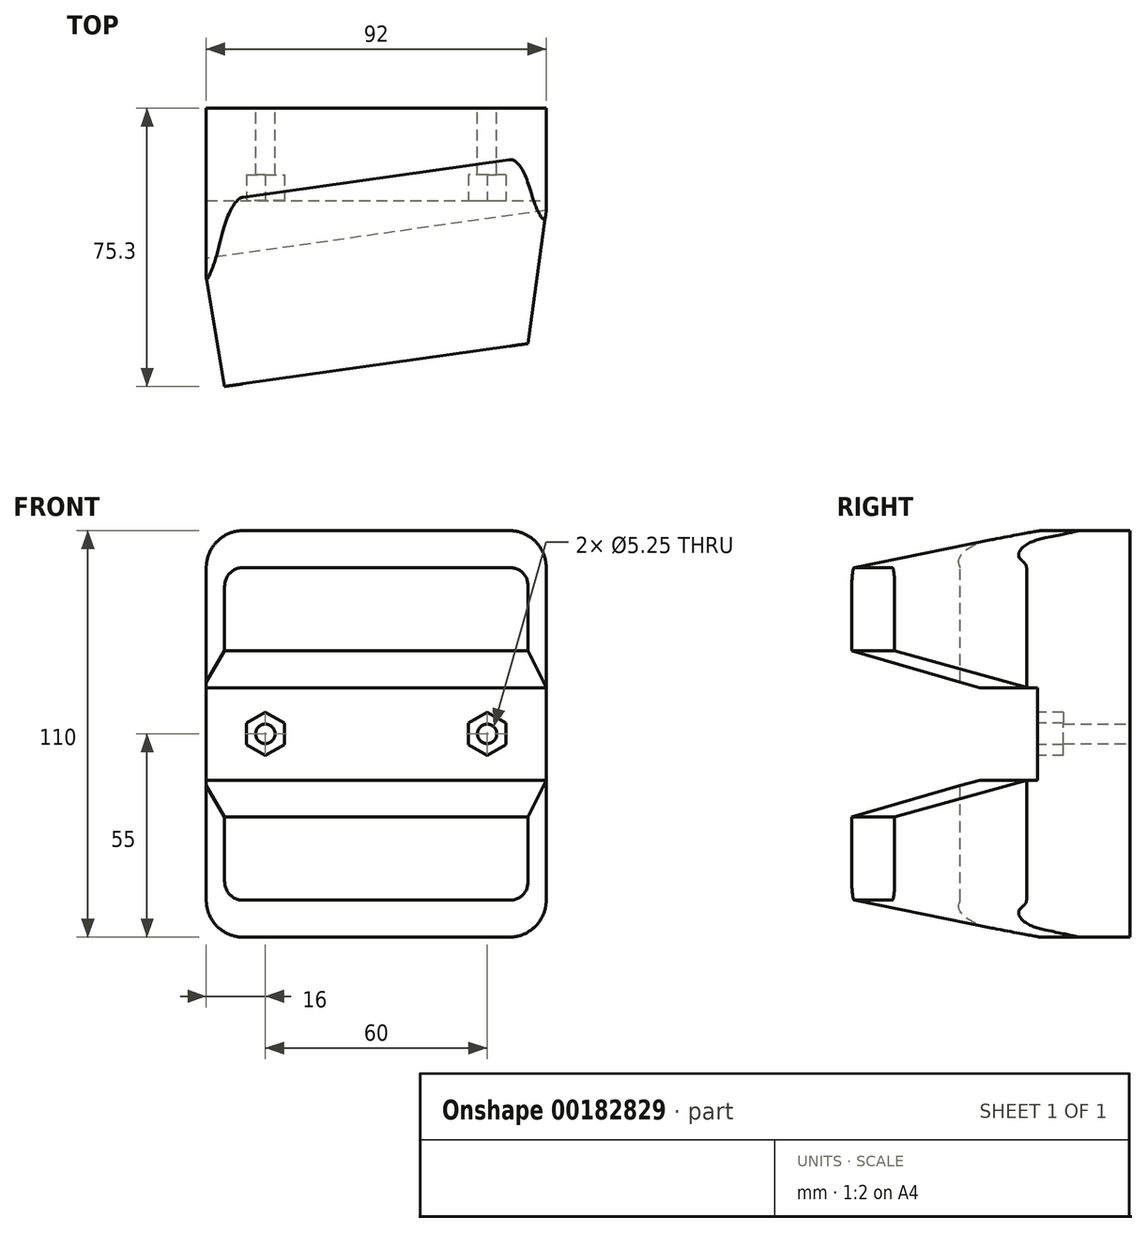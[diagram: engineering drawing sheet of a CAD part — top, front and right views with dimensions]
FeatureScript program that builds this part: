
annotation { "Feature Type Name" : "Feature", "Feature Type Description" : "" }
export const myFeature = defineFeature(function(context is Context, id is Id, definition is map)
    precondition{}
    {
        {
            var Q0;
            Q0=qCreatedBy(makeId("Top.planeOp"),FACE);
            var sketch = newSketch(context, id + "F0", { "sketchPlane" : qUnion([Q0])});
            skLineSegment(sketch, "E0", {"start": v(-46, 43.07) * mm, "end": v(46, 43.07) * mm});
            skLineSegment(sketch, "E1", {"start": v(46, 43.07) * mm, "end": v(46, -19.93) * mm});
            skLineSegment(sketch, "E2", {"start": v(46, -19.93) * mm, "end": v(-46, -32.93) * mm});
            skLineSegment(sketch, "E3", {"start": v(-46, -32.93) * mm, "end": v(-46, 43.07) * mm});
            skSolve(sketch);
        }
        {
            var Q0;
            Q0 = qSketchRegion(id + "F0", true);
            extrude(context, id + "F1", {"entities" : qUnion([Q0]), "depth" : 110 * mm});
        }
        {
            var Q0;
            Q0=makeQuery(id+"F1.opExtrude","SWEPT_FACE",FACE,{"disambiguationData":[OSD([sQuery(id+"F0.wireOp",EDGE,"E0")])]});
            cPlane(context, id + "F2", {"entities" : qUnion([Q0]), "cplaneType" : CPlaneType.OFFSET, "offset" : 25 * mm, "oppositeDirection" : true, "width" : 150 * mm, "height" : 150 * mm});
        }
        {
            var Q0;
            Q0=qCreatedBy(id+"F2.planeOp",FACE);
            var sketch = newSketch(context, id + "F3", { "sketchPlane" : qUnion([Q0])});
            skLineSegment(sketch, "E4.bottom", {"start": v(46, 67.5) * mm, "end": v(-46, 67.5) * mm});
            skLineSegment(sketch, "E4.top", {"start": v(46, 42.5) * mm, "end": v(-46, 42.5) * mm});
            skLineSegment(sketch, "E4.left", {"start": v(46, 67.5) * mm, "end": v(46, 42.5) * mm});
            skLineSegment(sketch, "E4.right", {"start": v(-46, 67.5) * mm, "end": v(-46, 42.5) * mm});
            skSolve(sketch);
        }
        {
            var Q0;
            Q0 = qSketchRegion(id + "F3", true);
            extrude(context, id + "F4", {"entities" : qUnion([Q0]), "operationType" : NewBodyOperationType.REMOVE, "oppositeDirection" : true, "depth" : 80 * mm});
        }
        {
            var Q0;
            Q0=makeQuery(id+"F1.opExtrude","CAP_EDGE",EDGE,{"disambiguationData":[OSD([sQuery(id+"F0.wireOp",EDGE,"E2")])],"isStart":false});
            chamfer(context, id + "F5", {"entities" : qUnion([Q0]), "chamferType" : ChamferType.TWO_OFFSETS, "width1" : 50 * mm, "oppositeDirection" : true, "width2" : 10 * mm, "tangentPropagation" : true});
        }
        {
            var Q0;
            Q0=makeQuery(id+"F1.opExtrude","CAP_EDGE",EDGE,{"disambiguationData":[OSD([sQuery(id+"F0.wireOp",EDGE,"E2")])],"isStart":true});
            chamfer(context, id + "F6", {"entities" : qUnion([Q0]), "chamferType" : ChamferType.TWO_OFFSETS, "width1" : 50 * mm, "oppositeDirection" : false, "width2" : 10 * mm, "tangentPropagation" : true});
        }
        {
            var Q0;
            Q0=makeQuery(id+"F4.boolean.opBoolean","INTERSECT",EDGE,{"derivedFrom":[makeQuery(id+"F1.opExtrude","SWEPT_FACE",FACE,{"disambiguationData":[OSD([sQuery(id+"F0.wireOp",EDGE,"E2")])]}),makeQuery(id+"F4.opExtrude","SWEPT_FACE",FACE,{"disambiguationData":[OSD([sQuery(id+"F3.wireOp",EDGE,"E4.bottom")])]})]});
            chamfer(context, id + "F7", {"entities" : qUnion([Q0]), "chamferType" : ChamferType.TWO_OFFSETS, "width1" : 35 * mm, "oppositeDirection" : false, "width2" : 10 * mm, "tangentPropagation" : true});
        }
        {
            var Q0;
            Q0=makeQuery(id+"F4.boolean.opBoolean","INTERSECT",EDGE,{"derivedFrom":[makeQuery(id+"F1.opExtrude","SWEPT_FACE",FACE,{"disambiguationData":[OSD([sQuery(id+"F0.wireOp",EDGE,"E2")])]}),makeQuery(id+"F4.opExtrude","SWEPT_FACE",FACE,{"disambiguationData":[OSD([sQuery(id+"F3.wireOp",EDGE,"E4.top")])]})]});
            chamfer(context, id + "F8", {"entities" : qUnion([Q0]), "chamferType" : ChamferType.TWO_OFFSETS, "width1" : 35 * mm, "oppositeDirection" : true, "width2" : 10 * mm, "tangentPropagation" : true});
        }
        {
            var Q0;
            {var subQ0=sQuery(id+"F0.wireOp",EDGE,"E2");var subQ1=sQuery(id+"F0.wireOp",EDGE,"E1");Q0=makeQuery(id+"F4.boolean.opBoolean","SPLIT",EDGE,{"disambiguationData":[TD([makeQuery(id+"F4.opExtrude","SWEPT_FACE",FACE,{"disambiguationData":[OSD([sQuery(id+"F3.wireOp",EDGE,"E4.top")])]})])],"derivedFrom":makeQuery(id+"F1.opExtrude","SWEPT_EDGE",EDGE,{"disambiguationData":[OSD([subQ1,subQ0])]})});}
            var Q1;
            {var subQ0=sQuery(id+"F0.wireOp",EDGE,"E2");var subQ1=sQuery(id+"F0.wireOp",EDGE,"E1");Q1=makeQuery(id+"F4.boolean.opBoolean","SPLIT",EDGE,{"disambiguationData":[TD([makeQuery(id+"F4.opExtrude","SWEPT_FACE",FACE,{"disambiguationData":[OSD([sQuery(id+"F3.wireOp",EDGE,"E4.bottom")])]})])],"derivedFrom":makeQuery(id+"F1.opExtrude","SWEPT_EDGE",EDGE,{"disambiguationData":[OSD([subQ1,subQ0])]})});}
            chamfer(context, id + "F9", {"entities" : qUnion([Q0, Q1]), "chamferType" : ChamferType.TWO_OFFSETS, "width1" : 35 * mm, "oppositeDirection" : false, "width2" : 5 * mm, "tangentPropagation" : true});
        }
        {
            var Q0;
            {var subQ0=sQuery(id+"F0.wireOp",EDGE,"E3");var subQ1=sQuery(id+"F0.wireOp",EDGE,"E2");Q0=makeQuery(id+"F4.boolean.opBoolean","SPLIT",EDGE,{"disambiguationData":[TD([makeQuery(id+"F4.opExtrude","SWEPT_FACE",FACE,{"disambiguationData":[OSD([sQuery(id+"F3.wireOp",EDGE,"E4.bottom")])]})])],"derivedFrom":makeQuery(id+"F1.opExtrude","SWEPT_EDGE",EDGE,{"disambiguationData":[OSD([subQ1,subQ0])]})});}
            var Q1;
            {var subQ0=sQuery(id+"F0.wireOp",EDGE,"E3");var subQ1=sQuery(id+"F0.wireOp",EDGE,"E2");Q1=makeQuery(id+"F4.boolean.opBoolean","SPLIT",EDGE,{"disambiguationData":[TD([makeQuery(id+"F4.opExtrude","SWEPT_FACE",FACE,{"disambiguationData":[OSD([sQuery(id+"F3.wireOp",EDGE,"E4.top")])]})])],"derivedFrom":makeQuery(id+"F1.opExtrude","SWEPT_EDGE",EDGE,{"disambiguationData":[OSD([subQ1,subQ0])]})});}
            chamfer(context, id + "F10", {"entities" : qUnion([Q0, Q1]), "chamferType" : ChamferType.TWO_OFFSETS, "width1" : 30 * mm, "oppositeDirection" : true, "width2" : 5 * mm, "tangentPropagation" : true});
        }
        {
            var Q0;
            Q0=makeQuery(id+"F1.opExtrude","CAP_EDGE",EDGE,{"disambiguationData":[OSD([sQuery(id+"F0.wireOp",EDGE,"E3")])],"isStart":false});
            var Q1;
            Q1=makeQuery(id+"F1.opExtrude","CAP_EDGE",EDGE,{"disambiguationData":[OSD([sQuery(id+"F0.wireOp",EDGE,"E3")])],"isStart":true});
            var Q2;
            Q2=makeQuery(id+"F1.opExtrude","CAP_EDGE",EDGE,{"disambiguationData":[OSD([sQuery(id+"F0.wireOp",EDGE,"E1")])],"isStart":true});
            var Q3;
            Q3=makeQuery(id+"F1.opExtrude","CAP_EDGE",EDGE,{"disambiguationData":[OSD([sQuery(id+"F0.wireOp",EDGE,"E1")])],"isStart":false});
            fillet(context, id + "F11", {"entities" : qUnion([Q0, Q1, Q2, Q3]), "radius" : 10 * mm, "tangentPropagation" : true, "allowEdgeOverflow" : false});
        }
        {
            var Q0;
            {var subQ0=sQuery(id+"F0.wireOp",EDGE,"E2");var subQ1=sQuery(id+"F0.wireOp",EDGE,"E3");Q0=makeQuery(id+"F10.opChamfer","BLEND_EDGE",EDGE,{"blendedFrom":[makeQuery(id+"F4.boolean.opBoolean","SPLIT",EDGE,{"disambiguationData":[TD([makeQuery(id+"F4.opExtrude","SWEPT_FACE",FACE,{"disambiguationData":[OSD([sQuery(id+"F3.wireOp",EDGE,"E4.top")])]})])],"derivedFrom":makeQuery(id+"F1.opExtrude","SWEPT_EDGE",EDGE,{"disambiguationData":[OSD([subQ0,subQ1])]})}),makeQuery(id+"F6.opChamfer","BLEND_FACE",FACE,{"disambiguationData":[OSD([subQ0])]})],"blendedInto":[makeQuery(id+"F6.opChamfer","BLEND_FACE",FACE,{"disambiguationData":[OSD([subQ0])]})]});}
            var Q1;
            {var subQ0=sQuery(id+"F0.wireOp",EDGE,"E2");var subQ1=sQuery(id+"F0.wireOp",EDGE,"E1");Q1=makeQuery(id+"F9.opChamfer","BLEND_EDGE",EDGE,{"blendedFrom":[makeQuery(id+"F4.boolean.opBoolean","SPLIT",EDGE,{"disambiguationData":[TD([makeQuery(id+"F4.opExtrude","SWEPT_FACE",FACE,{"disambiguationData":[OSD([sQuery(id+"F3.wireOp",EDGE,"E4.top")])]})])],"derivedFrom":makeQuery(id+"F1.opExtrude","SWEPT_EDGE",EDGE,{"disambiguationData":[OSD([subQ1,subQ0])]})}),makeQuery(id+"F6.opChamfer","BLEND_FACE",FACE,{"disambiguationData":[OSD([subQ0])]})],"blendedInto":[makeQuery(id+"F6.opChamfer","BLEND_FACE",FACE,{"disambiguationData":[OSD([subQ0])]})]});}
            var Q2;
            {var subQ0=sQuery(id+"F0.wireOp",EDGE,"E2");var subQ1=sQuery(id+"F0.wireOp",EDGE,"E1");Q2=makeQuery(id+"F9.opChamfer","BLEND_EDGE",EDGE,{"blendedFrom":[makeQuery(id+"F4.boolean.opBoolean","SPLIT",EDGE,{"disambiguationData":[TD([makeQuery(id+"F4.opExtrude","SWEPT_FACE",FACE,{"disambiguationData":[OSD([sQuery(id+"F3.wireOp",EDGE,"E4.bottom")])]})])],"derivedFrom":makeQuery(id+"F1.opExtrude","SWEPT_EDGE",EDGE,{"disambiguationData":[OSD([subQ1,subQ0])]})}),makeQuery(id+"F5.opChamfer","BLEND_FACE",FACE,{"disambiguationData":[OSD([subQ0])]})],"blendedInto":[makeQuery(id+"F5.opChamfer","BLEND_FACE",FACE,{"disambiguationData":[OSD([subQ0])]})]});}
            var Q3;
            {var subQ0=sQuery(id+"F0.wireOp",EDGE,"E2");var subQ1=sQuery(id+"F0.wireOp",EDGE,"E3");Q3=makeQuery(id+"F10.opChamfer","BLEND_EDGE",EDGE,{"blendedFrom":[makeQuery(id+"F4.boolean.opBoolean","SPLIT",EDGE,{"disambiguationData":[TD([makeQuery(id+"F4.opExtrude","SWEPT_FACE",FACE,{"disambiguationData":[OSD([sQuery(id+"F3.wireOp",EDGE,"E4.bottom")])]})])],"derivedFrom":makeQuery(id+"F1.opExtrude","SWEPT_EDGE",EDGE,{"disambiguationData":[OSD([subQ0,subQ1])]})}),makeQuery(id+"F5.opChamfer","BLEND_FACE",FACE,{"disambiguationData":[OSD([subQ0])]})],"blendedInto":[makeQuery(id+"F5.opChamfer","BLEND_FACE",FACE,{"disambiguationData":[OSD([subQ0])]})]});}
            fillet(context, id + "F12", {"entities" : qUnion([Q0, Q1, Q2, Q3]), "radius" : 5 * mm, "tangentPropagation" : true, "allowEdgeOverflow" : false});
        }
        {
            var Q0;
            Q0=makeQuery(id+"F1.opExtrude","SWEPT_FACE",FACE,{"disambiguationData":[OSD([sQuery(id+"F0.wireOp",EDGE,"E0")])]});
            var sketch = newSketch(context, id + "F13", { "sketchPlane" : qUnion([Q0])});
            skLineSegment(sketch, "E5", {"start": v(-47.9, 55) * mm, "end": v(51.83, 55) * mm});
            skPoint(sketch, "E6", {"position": v(-30, 55) * mm});
            skPoint(sketch, "E7", {"position": v(30, 55) * mm});
            skSolve(sketch);
        }
        {
            var Q0;
            Q0=sQuery(id+"F13.wireOp",VERTEX,"E6");
            var Q1;
            Q1=sQuery(id+"F13.wireOp",VERTEX,"E7");
            var Q2;
            Q2=makeQuery(id+"F1.opExtrude","SWEPT_BODY",BODY,{"disambiguationData":[OSD([sQuery(id+"F0.wireOp",EDGE,"E0"),sQuery(id+"F0.wireOp",EDGE,"E1"),sQuery(id+"F0.wireOp",EDGE,"E2"),sQuery(id+"F0.wireOp",EDGE,"E3")])]});
            hole(context, id + "F14", {"style" : HoleStyle.SIMPLE, "endStyle" : HoleEndStyle.THROUGH, "holeDiameter" : 5.25 * mm, "startFromSketch" : true, "locations" : qUnion([Q0, Q1]), "scope" : qUnion([Q2]), "isTappedThrough" : true});
        }
        {
            var Q0;
            Q0=makeQuery(id+"F4.boolean.opBoolean","COPY",FACE,{"derivedFrom":makeQuery(id+"F4.opExtrude","CAP_FACE",FACE,{"disambiguationData":[OSD([sQuery(id+"F3.wireOp",EDGE,"E4.bottom"),sQuery(id+"F3.wireOp",EDGE,"E4.top"),sQuery(id+"F3.wireOp",EDGE,"E4.left"),sQuery(id+"F3.wireOp",EDGE,"E4.right")])],"isStart":true})});
            var sketch = newSketch(context, id + "F15", { "sketchPlane" : qUnion([Q0])});
            skCircle(sketch, "E8.cCircle", {"center": v(-30, 55) * mm, "radius": 5.1 * mm, "construction": true});
            skLineSegment(sketch, "E8.0", {"start": v(-24.9, 57.94) * mm, "end": v(-24.9, 52.06) * mm});
            skLineSegment(sketch, "E8.1", {"start": v(-24.9, 52.06) * mm, "end": v(-30, 49.11) * mm});
            skLineSegment(sketch, "E8.2", {"start": v(-30, 49.11) * mm, "end": v(-35.1, 52.06) * mm});
            skLineSegment(sketch, "E8.3", {"start": v(-35.1, 52.06) * mm, "end": v(-35.1, 57.94) * mm});
            skLineSegment(sketch, "E8.4", {"start": v(-35.1, 57.94) * mm, "end": v(-30, 60.89) * mm});
            skLineSegment(sketch, "E8.5", {"start": v(-30, 60.89) * mm, "end": v(-24.9, 57.94) * mm});
            skPoint(sketch, "E8.0.midPoint", {"position": v(-24.9, 55) * mm});
            skCircle(sketch, "E9.cCircle", {"center": v(30, 55) * mm, "radius": 5.1 * mm, "construction": true});
            skLineSegment(sketch, "E9.0", {"start": v(24.9, 52.06) * mm, "end": v(24.9, 57.94) * mm});
            skLineSegment(sketch, "E9.1", {"start": v(24.9, 57.94) * mm, "end": v(30, 60.89) * mm});
            skLineSegment(sketch, "E9.2", {"start": v(30, 60.89) * mm, "end": v(35.1, 57.94) * mm});
            skLineSegment(sketch, "E9.3", {"start": v(35.1, 57.94) * mm, "end": v(35.1, 52.06) * mm});
            skLineSegment(sketch, "E9.4", {"start": v(35.1, 52.06) * mm, "end": v(30, 49.11) * mm});
            skLineSegment(sketch, "E9.5", {"start": v(30, 49.11) * mm, "end": v(24.9, 52.06) * mm});
            skPoint(sketch, "E9.0.midPoint", {"position": v(24.9, 55) * mm});
            skSolve(sketch);
        }
        {
            var Q0;
            Q0 = qSketchRegion(id + "F15", true);
            extrude(context, id + "F16", {"entities" : qUnion([Q0]), "operationType" : NewBodyOperationType.REMOVE, "oppositeDirection" : true, "depth" : 7 * mm});
        }
    });
